# Revit family: Building-ConnessioniIEC309-GEWISS-COMBIBLOC-PRESE-INTERBLOCCATE_IP44_SENZA_FONDO
name_source: partatom
category: Apparecchi elettrici
units: mm (PartAtom-declared; Revit-internal decimal feet)

## family parameters
Condiviso = No
Host = Superficie
Mantenere orientamento annotazione = Sì
Punto di calcolo locali = Sì
Quota connettore circolare = Usa diametro
Taglio con vuoti quando caricato = No
Tipo di parte = Normale

## types (18) — shared parameters
BLOCCO = B=C
Catalogo = BUILDING
Codice Electrocod = 2220
Con fondo = No
FORMULA = 1000 mm  [stored 3.28084 ft]
Frequenza = 50/60 Hz
Glow wire test: = 850 °C (Parti attive) - 650 °C (Parti passive)
Grado di protezione = IP44
IDF = 31259a23-73b2-4997-9df9-78b802d9498e
IDT = 741e4717e3ee4884b61990f959ff1807
Immagine tipo = COMBIBLOC44.jpg
L = 155 mm
N.poli = 1
POMELLO = bianco
PRESA = Giallo
Produttore = GEWISS S.p.A.
Prospetto di default = 1219 mm
Protezione = NO (SBF)
Resistenza agli urti = IK08
SEO = Presa interbloccata
STRUTTURA = RAL - 7035
STRUTTURA ALTA = blue
Scheda Tecnica = https://www.gewiss.com
Spostamento_S = 1500 mm
Temperatura di utilizzo = -25 +40 °C
Termopressione con biglia = 125 °C
Tipologia = Compatta
URL = https://www.gewiss.com
VETRO = Vetro
Versione file RFA = 21.4
Voltaggio = 0 V
W = 115 mm

## per-type parameters (varying)
| type | Colore: | Corrente nominale (A) | Descrizione | Modello | N. poli | Riferimento h | Tensione nominale |
| GW66430 - COMBIBLOC S.F.IP44 3P+T 16A 400V 6H | Rosso | 16 | COMBIBLOC S.F.IP44 3P+T 16A 400V 6H | GW66430 | 3P+T | 6 | 380-415V |
| GW66425 - COMBIBLOC S.F.IP44 3P+N+T 16A 110V 4H | Giallo | 16 | COMBIBLOC S.F.IP44 3P+N+T 16A 110V 4H | GW66425 | 3P+N+T | 4 | 100-130V |
| GW66434 - COMBIBLOC S.F.IP44 2P+T 32A 110V 4H | Giallo | 32 | COMBIBLOC S.F.IP44 2P+T 32A 110V 4H | GW66434 | 2P+T | 4 | 100-130V |
| GW66429 - COMBIBLOC S.F.IP44 2P+T 16A 400V 9H | Rosso | 16 | COMBIBLOC S.F.IP44 2P+T 16A 400V 9H | GW66429 | 2P+T | 9 | 380-415V |
| GW66423 - COMBIBLOC S.F.IP44 2P+T 16A 110V 4H | Giallo | 16 | COMBIBLOC S.F.IP44 2P+T 16A 110V 4H | GW66423 | 2P+T | 4 | 100-130V |
| GW66436 - COMBIBLOC S.F.IP44 3P+N+T 32A 110V 4H | Giallo | 32 | COMBIBLOC S.F.IP44 3P+N+T 32A 110V 4H | GW66436 | 3P+N+T | 4 | 100-130V |
| GW66438 - COMBIBLOC S.F.IP44 3P+T 32A 230V 9H | Blu | 32 | COMBIBLOC S.F.IP44 3P+T 32A 230V 9H | GW66438 | 3P+T | 9 | 200-250V |
| GW66441 - COMBIBLOC S.F.IP44 3P+T 32A 400V 6H | Rosso | 32 | COMBIBLOC S.F.IP44 3P+T 32A 400V 6H | GW66441 | 3P+T | 6 | 380-415V |
| GW66427 - COMBIBLOC S.F.IP44 3P+T 16A 230V 9H | Blu | 16 | COMBIBLOC S.F.IP44 3P+T 16A 230V 9H | GW66427 | 3P+T | 9 | 200-250V |
| GW66431 - COMBIBLOC S.F.IP44 3P+N+T 16A 400V 6H | Rosso | 16 | COMBIBLOC S.F.IP44 3P+N+T 16A 400V 6H | GW66431 | 3P+N+T | 6 | 380-415V |
| GW66424 - COMBIBLOC S.F.IP44 3P+T 16A 110V 4H | Giallo | 16 | COMBIBLOC S.F.IP44 3P+T 16A 110V 4H | GW66424 | 3P+T | 4 | 100-130V |
| GW66437 - COMBIBLOC S.F.IP44 2P+T 32A 230V 6H | Blu | 32 | COMBIBLOC S.F.IP44 2P+T 32A 230V 6H | GW66437 | 2P+T | 6 | 200-250V |
| GW66439 - COMBIBLOC S.F.IP44 3P+N+T 32A 230V 9H | Blu | 32 | COMBIBLOC S.F.IP44 3P+N+T 32A 230V 9H | GW66439 | 3P+N+T | 9 | 200-250V |
| GW66442 - COMBIBLOC S.F.IP44 3P+N+T 32A 400V 6H | Rosso | 32 | COMBIBLOC S.F.IP44 3P+N+T 32A 400V 6H | GW66442 | 3P+N+T | 6 | 380-415V |
| GW66440 - COMBIBLOC S.F.IP44 2P+T 32A 400V 9H | Rosso | 32 | COMBIBLOC S.F.IP44 2P+T 32A 400V 9H | GW66440 | 2P+T | 9 | 380-415V |
| GW66428 - COMBIBLOC S.F.IP44 3P+N+T 16A 230V 9H | Blu | 16 | COMBIBLOC S.F.IP44 3P+N+T 16A 230V 9H | GW66428 | 3P+N+T | 9 | 200-250V |
| GW66426 - COMBIBLOC S.F.IP44 2P+T 16A 230V 6H | Blu | 16 | COMBIBLOC S.F.IP44 2P+T 16A 230V 6H | GW66426 | 2P+T | 6 | 200-250V |
| GW66435 - COMBIBLOC S.F.IP44 3P+T 32A 110V 4H | Giallo | 32 | COMBIBLOC S.F.IP44 3P+T 32A 110V 4H | GW66435 | 3P+T | 4 | 100-130V |

note: [stored X ft] marks values corroborated as IEEE doubles in the binary element streams (Revit-internal decimal feet)

## geometry (parser evidence)
native form markers: Sweep x4
no freeform markers — native parametric forms only
